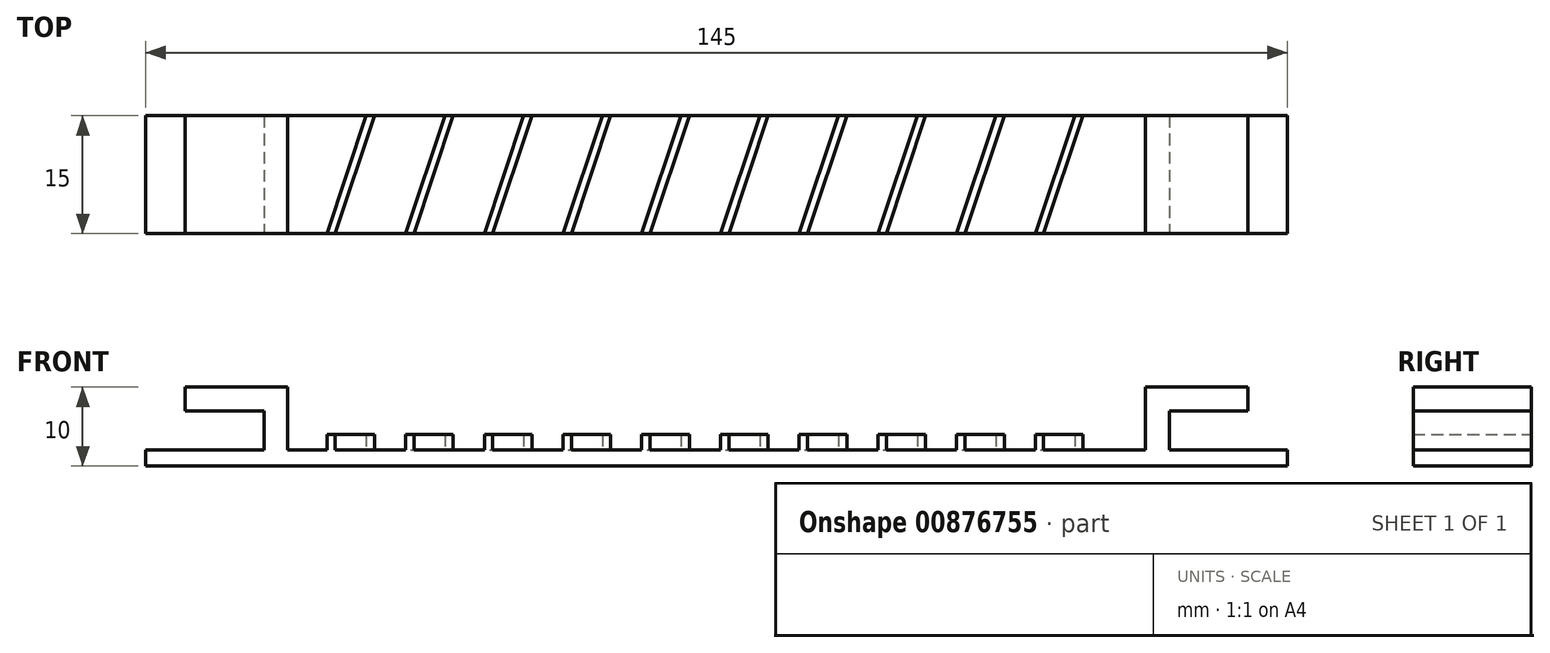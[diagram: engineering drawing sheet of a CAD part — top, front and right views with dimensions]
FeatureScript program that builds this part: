
annotation { "Feature Type Name" : "Feature", "Feature Type Description" : "" }
export const myFeature = defineFeature(function(context is Context, id is Id, definition is map)
    precondition{}
    {
        {
            var Q0;
            Q0=qCreatedBy(makeId("Top.planeOp"),FACE);
            var sketch = newSketch(context, id + "F0", { "sketchPlane" : qUnion([Q0])});
            skLineSegment(sketch, "E0.bottom", {"start": v(-72.5, 7.5) * mm, "end": v(72.5, 7.5) * mm});
            skLineSegment(sketch, "E0.top", {"start": v(-72.5, -7.5) * mm, "end": v(72.5, -7.5) * mm});
            skLineSegment(sketch, "E0.left", {"start": v(-72.5, 7.5) * mm, "end": v(-72.5, -7.5) * mm});
            skLineSegment(sketch, "E0.right", {"start": v(72.5, 7.5) * mm, "end": v(72.5, -7.5) * mm});
            skPoint(sketch, "E0.middle", {"position": v(0, 0) * mm});
            skSolve(sketch);
        }
        {
            var Q0;
            Q0 = qSketchRegion(id + "F0", true);
            extrude(context, id + "F1", {"entities" : qUnion([Q0]), "depth" : 2 * mm, "offsetDistance" : 25 * mm});
        }
        {
            var Q0;
            Q0=makeQuery(id+"F1.opExtrude","SWEPT_FACE",FACE,{"disambiguationData":[OSD([sQuery(id+"F0.wireOp",EDGE,"E0.top")])]});
            var sketch = newSketch(context, id + "F2", { "sketchPlane" : qUnion([Q0])});
            skLineSegment(sketch, "E1", {"start": v(-57.5, 2) * mm, "end": v(-57.5, 7) * mm});
            skLineSegment(sketch, "E2", {"start": v(-57.5, 7) * mm, "end": v(-67.5, 7) * mm});
            skLineSegment(sketch, "E3", {"start": v(-67.5, 7) * mm, "end": v(-67.5, 10) * mm});
            skLineSegment(sketch, "E4", {"start": v(-67.5, 10) * mm, "end": v(-54.5, 10) * mm});
            skLineSegment(sketch, "E5", {"start": v(-54.5, 10) * mm, "end": v(-54.5, 2) * mm});
            skLineSegment(sketch, "E6", {"start": v(-54.5, 2) * mm, "end": v(-57.5, 2) * mm});
            skLineSegment(sketch, "E7", {"start": v(0, 0) * mm, "end": v(0, 2) * mm, "construction": true});
            skLineSegment(sketch, "E8.MirrorCS", {"start": v(67.5, 7) * mm, "end": v(67.5, 10) * mm});
            skLineSegment(sketch, "E9.MirrorCS", {"start": v(57.5, 2) * mm, "end": v(57.5, 7) * mm});
            skLineSegment(sketch, "E10.MirrorCS", {"start": v(54.5, 2) * mm, "end": v(57.5, 2) * mm});
            skLineSegment(sketch, "E11.MirrorCS", {"start": v(67.5, 10) * mm, "end": v(54.5, 10) * mm});
            skLineSegment(sketch, "E12.MirrorCS", {"start": v(57.5, 7) * mm, "end": v(67.5, 7) * mm});
            skLineSegment(sketch, "E13.MirrorCS", {"start": v(54.5, 10) * mm, "end": v(54.5, 2) * mm});
            skSolve(sketch);
        }
        {
            var Q0;
            Q0 = qSketchRegion(id + "F2", true);
            var Q1;
            Q1=makeQuery(id+"F1.opExtrude","SWEPT_FACE",FACE,{"disambiguationData":[OSD([sQuery(id+"F0.wireOp",EDGE,"E0.bottom")])]});
            extrude(context, id + "F3", {"entities" : qUnion([Q0]), "operationType" : NewBodyOperationType.ADD, "endBound" : BoundingType.UP_TO_SURFACE, "oppositeDirection" : true, "depth" : 25 * mm, "endBoundEntityFace" : qUnion([Q1]), "offsetDistance" : 25 * mm});
        }
        {
            var Q0;
            {var subQ1=sQuery(id+"F2.wireOp",EDGE,"E5");var subQ6=sQuery(id+"F0.wireOp",EDGE,"E0.top");var subQ7=sQuery(id+"F0.wireOp",EDGE,"E0.bottom");Q0=makeQuery(id+"F3.boolean.opBoolean","SPLIT",FACE,{"disambiguationData":[TD([makeQuery(id+"F3.opExtrude","SWEPT_FACE",FACE,{"disambiguationData":[OSD([subQ1])]})])],"derivedFrom":makeQuery(id+"F1.opExtrude","CAP_FACE",FACE,{"disambiguationData":[OSD([subQ7,subQ6,sQuery(id+"F0.wireOp",EDGE,"E0.left"),sQuery(id+"F0.wireOp",EDGE,"E0.right")])],"isStart":false})});}
            var sketch = newSketch(context, id + "F4", { "sketchPlane" : qUnion([Q0])});
            skLineSegment(sketch, "E14", {"start": v(-49.5, -7.5) * mm, "end": v(-44.5, 7.5) * mm});
            skLineSegment(sketch, "E15", {"start": v(-44.5, 7.5) * mm, "end": v(-43.45, 7.5) * mm});
            skLineSegment(sketch, "E16", {"start": v(-43.45, 7.5) * mm, "end": v(-48.45, -7.5) * mm});
            skLineSegment(sketch, "E17", {"start": v(-48.45, -7.5) * mm, "end": v(-49.5, -7.5) * mm});
            skLineSegment(sketch, "E18.1.0.0", {"start": v(-39.5, -7.5) * mm, "end": v(-34.5, 7.5) * mm});
            skLineSegment(sketch, "E18.1.0.1", {"start": v(-34.5, 7.5) * mm, "end": v(-33.45, 7.5) * mm});
            skLineSegment(sketch, "E18.1.0.2", {"start": v(-33.45, 7.5) * mm, "end": v(-38.45, -7.5) * mm});
            skLineSegment(sketch, "E18.1.0.3", {"start": v(-38.45, -7.5) * mm, "end": v(-39.5, -7.5) * mm});
            skLineSegment(sketch, "E18.2.0.0", {"start": v(-29.5, -7.5) * mm, "end": v(-24.5, 7.5) * mm});
            skLineSegment(sketch, "E18.2.0.1", {"start": v(-24.5, 7.5) * mm, "end": v(-23.45, 7.5) * mm});
            skLineSegment(sketch, "E18.2.0.2", {"start": v(-23.45, 7.5) * mm, "end": v(-28.45, -7.5) * mm});
            skLineSegment(sketch, "E18.2.0.3", {"start": v(-28.45, -7.5) * mm, "end": v(-29.5, -7.5) * mm});
            skLineSegment(sketch, "E18.3.0.0", {"start": v(-19.5, -7.5) * mm, "end": v(-14.5, 7.5) * mm});
            skLineSegment(sketch, "E18.3.0.1", {"start": v(-14.5, 7.5) * mm, "end": v(-13.45, 7.5) * mm});
            skLineSegment(sketch, "E18.3.0.2", {"start": v(-13.45, 7.5) * mm, "end": v(-18.45, -7.5) * mm});
            skLineSegment(sketch, "E18.3.0.3", {"start": v(-18.45, -7.5) * mm, "end": v(-19.5, -7.5) * mm});
            skLineSegment(sketch, "E18.4.0.0", {"start": v(-9.5, -7.5) * mm, "end": v(-4.5, 7.5) * mm});
            skLineSegment(sketch, "E18.4.0.1", {"start": v(-4.5, 7.5) * mm, "end": v(-3.45, 7.5) * mm});
            skLineSegment(sketch, "E18.4.0.2", {"start": v(-3.45, 7.5) * mm, "end": v(-8.45, -7.5) * mm});
            skLineSegment(sketch, "E18.4.0.3", {"start": v(-8.45, -7.5) * mm, "end": v(-9.5, -7.5) * mm});
            skLineSegment(sketch, "E18.5.0.0", {"start": v(0.5, -7.5) * mm, "end": v(5.5, 7.5) * mm});
            skLineSegment(sketch, "E18.5.0.1", {"start": v(5.5, 7.5) * mm, "end": v(6.55, 7.5) * mm});
            skLineSegment(sketch, "E18.5.0.2", {"start": v(6.55, 7.5) * mm, "end": v(1.55, -7.5) * mm});
            skLineSegment(sketch, "E18.5.0.3", {"start": v(1.55, -7.5) * mm, "end": v(0.5, -7.5) * mm});
            skLineSegment(sketch, "E18.6.0.0", {"start": v(10.5, -7.5) * mm, "end": v(15.5, 7.5) * mm});
            skLineSegment(sketch, "E18.6.0.1", {"start": v(15.5, 7.5) * mm, "end": v(16.55, 7.5) * mm});
            skLineSegment(sketch, "E18.6.0.2", {"start": v(16.55, 7.5) * mm, "end": v(11.55, -7.5) * mm});
            skLineSegment(sketch, "E18.6.0.3", {"start": v(11.55, -7.5) * mm, "end": v(10.5, -7.5) * mm});
            skLineSegment(sketch, "E18.7.0.0", {"start": v(20.5, -7.5) * mm, "end": v(25.5, 7.5) * mm});
            skLineSegment(sketch, "E18.7.0.1", {"start": v(25.5, 7.5) * mm, "end": v(26.55, 7.5) * mm});
            skLineSegment(sketch, "E18.7.0.2", {"start": v(26.55, 7.5) * mm, "end": v(21.55, -7.5) * mm});
            skLineSegment(sketch, "E18.7.0.3", {"start": v(21.55, -7.5) * mm, "end": v(20.5, -7.5) * mm});
            skLineSegment(sketch, "E18.8.0.0", {"start": v(30.5, -7.5) * mm, "end": v(35.5, 7.5) * mm});
            skLineSegment(sketch, "E18.8.0.1", {"start": v(35.5, 7.5) * mm, "end": v(36.55, 7.5) * mm});
            skLineSegment(sketch, "E18.8.0.2", {"start": v(36.55, 7.5) * mm, "end": v(31.55, -7.5) * mm});
            skLineSegment(sketch, "E18.8.0.3", {"start": v(31.55, -7.5) * mm, "end": v(30.5, -7.5) * mm});
            skLineSegment(sketch, "E18.9.0.0", {"start": v(40.5, -7.5) * mm, "end": v(45.5, 7.5) * mm});
            skLineSegment(sketch, "E18.9.0.1", {"start": v(45.5, 7.5) * mm, "end": v(46.55, 7.5) * mm});
            skLineSegment(sketch, "E18.9.0.2", {"start": v(46.55, 7.5) * mm, "end": v(41.55, -7.5) * mm});
            skLineSegment(sketch, "E18.9.0.3", {"start": v(41.55, -7.5) * mm, "end": v(40.5, -7.5) * mm});
            skLineSegment(sketch, "E18.direction1", {"start": v(-49.5, -7.5) * mm, "end": v(-39.5, -7.5) * mm, "construction": true});
            skSolve(sketch);
        }
        {
            var Q0;
            Q0 = qSketchRegion(id + "F4", true);
            extrude(context, id + "F5", {"entities" : qUnion([Q0]), "operationType" : NewBodyOperationType.ADD, "depth" : 2 * mm, "offsetDistance" : 25 * mm});
        }
    });
